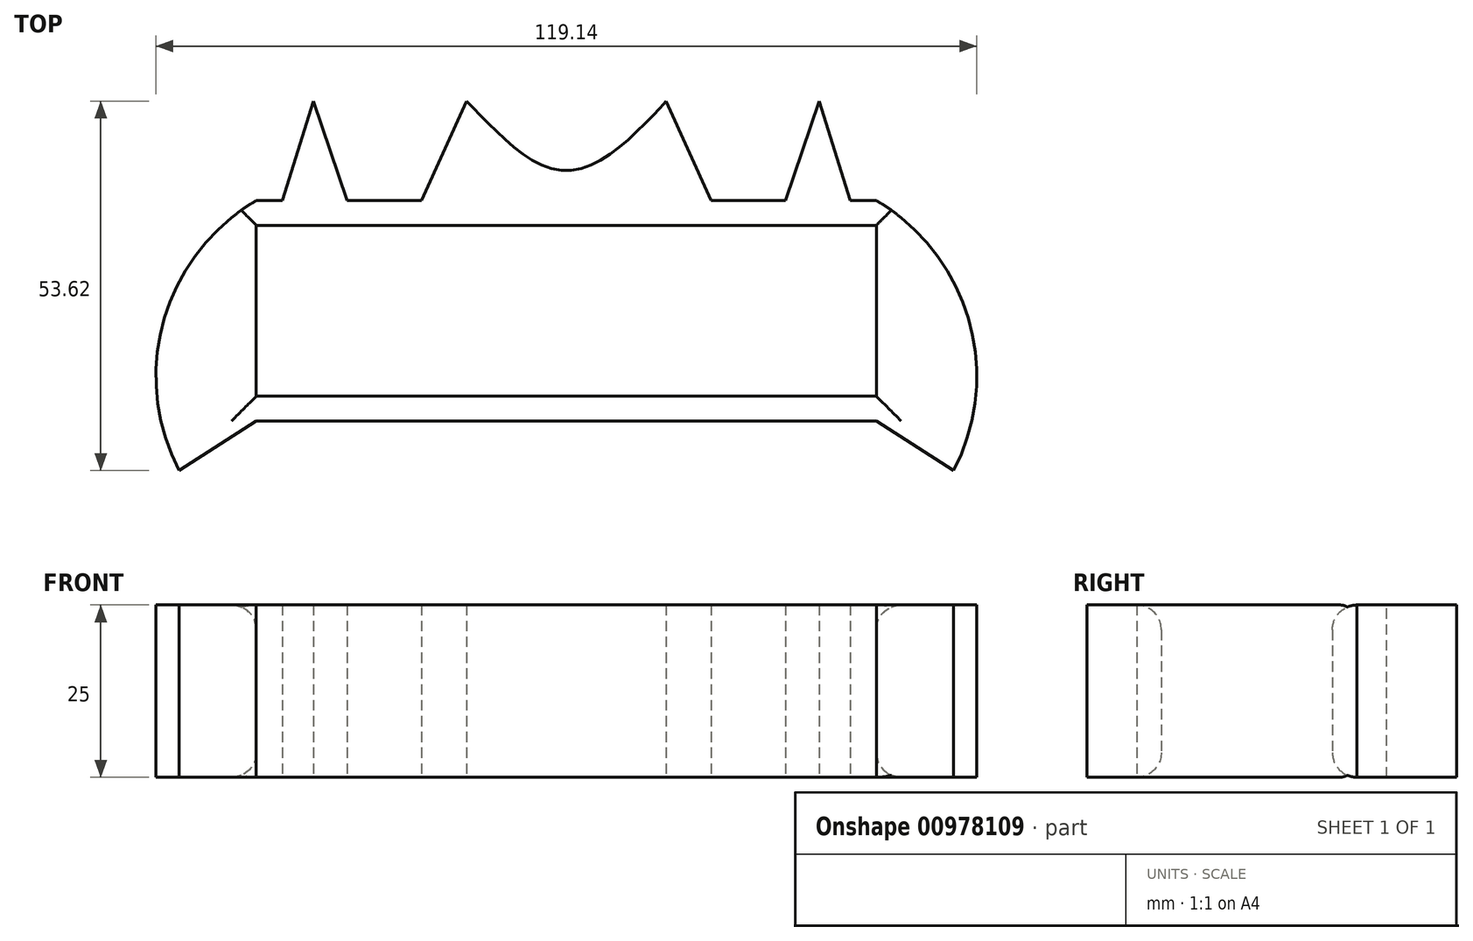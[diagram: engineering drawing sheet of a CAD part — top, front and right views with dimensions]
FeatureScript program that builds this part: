
annotation { "Feature Type Name" : "Feature", "Feature Type Description" : "" }
export const myFeature = defineFeature(function(context is Context, id is Id, definition is map)
    precondition{}
    {
        {
            var Q0;
            Q0=qCreatedBy(makeId("Top.planeOp"),FACE);
            var sketch = newSketch(context, id + "F0", { "sketchPlane" : qUnion([Q0])});
            skLineSegment(sketch, "E0.bottom", {"start": v(45, -16) * mm, "end": v(-45, -16) * mm});
            skLineSegment(sketch, "E0.top", {"start": v(45, 16) * mm, "end": v(-45, 16) * mm});
            skLineSegment(sketch, "E0.left", {"start": v(45, -16) * mm, "end": v(45, 16) * mm});
            skLineSegment(sketch, "E0.right", {"start": v(-45, -16) * mm, "end": v(-45, 16) * mm});
            skPoint(sketch, "E0.middle", {"position": v(0, 0) * mm});
            skPoint(sketch, "E1.centerSnap0", {"position": v(-45, 0) * mm});
            skFitSpline(sketch, "E2", {"points": [v(-14.5, 30.42) * mm, v(0, 20.32) * mm, v(14.5, 30.42) * mm], "startDerivative": vector(21.98, -21.4) * mm, "endDerivative": vector(20.35, 21.58) * mm});
            skLineSegment(sketch, "E3", {"start": v(14.5, 30.42) * mm, "end": v(21, 16) * mm});
            skLineSegment(sketch, "E4.MirrorCS", {"start": v(-14.5, 30.42) * mm, "end": v(-21, 16) * mm});
            skArc(sketch, "E5", {"start": v(56.2, -23.2) * mm, "mid": v(58.43, -1.36) * mm, "end": v(45, 16) * mm});
            skLineSegment(sketch, "E6", {"start": v(45, -16) * mm, "end": v(56.2, -23.2) * mm});
            skArc(sketch, "E7.MirrorCS", {"start": v(-56.2, -23.2) * mm, "mid": v(-58.43, -1.36) * mm, "end": v(-45, 16) * mm});
            skLineSegment(sketch, "E8.MirrorCS", {"start": v(-45, -16) * mm, "end": v(-56.2, -23.2) * mm});
            skLineSegment(sketch, "E9", {"start": v(-45, 12.4) * mm, "end": v(45, 12.4) * mm});
            skLineSegment(sketch, "E10", {"start": v(45, -12.4) * mm, "end": v(-45, -12.4) * mm});
            skPoint(sketch, "E11.end.orphan", {"position": v(-37, 16) * mm});
            skPoint(sketch, "E12.end.orphan", {"position": v(-43.48, 30.42) * mm});
            skPoint(sketch, "E12.start.orphan", {"position": v(-50, 16) * mm});
            skPoint(sketch, "E13.MirrorCS.end.orphan", {"position": v(43.48, 30.42) * mm});
            skPoint(sketch, "E13.MirrorCS.start.orphan", {"position": v(50, 16) * mm});
            skPoint(sketch, "E14.MirrorCS.end.orphan", {"position": v(37, 16) * mm});
            skLineSegment(sketch, "E15", {"start": v(-41.22, 16) * mm, "end": v(-36.7, 30.42) * mm});
            skLineSegment(sketch, "E16", {"start": v(-36.7, 30.42) * mm, "end": v(-31.81, 16) * mm});
            skLineSegment(sketch, "E17.MirrorCS", {"start": v(36.7, 30.42) * mm, "end": v(31.81, 16) * mm});
            skLineSegment(sketch, "E18.MirrorCS", {"start": v(41.22, 16) * mm, "end": v(36.7, 30.42) * mm});
            skPoint(sketch, "E19.MirrorC.center.orphan", {"position": v(14.5, 0) * mm});
            skPoint(sketch, "E1.center.orphan", {"position": v(-43.5, 0) * mm});
            skPoint(sketch, "E20.center.orphan", {"position": v(-14.5, 0) * mm});
            skSolve(sketch);
        }
        {
            var Q0;
            Q0=makeQuery(id+"F0.imprint","IMPRINT",FACE,{"disambiguationData":[TD([[makeQuery(id+"F0.imprint","IMPRINT",EDGE,{"derivedFrom":sQuery(id+"F0.wireOp",EDGE,"E0.right")}),1.0]])]});
            var Q1;
            Q1=makeQuery(id+"F0.imprint","IMPRINT",FACE,{"disambiguationData":[TD([[makeQuery(id+"F0.imprint","IMPRINT",EDGE,{"derivedFrom":sQuery(id+"F0.wireOp",EDGE,"E0.bottom")}),-1.0]])]});
            var Q2;
            {var subQ0=sQuery(id+"F0.wireOp",EDGE,"E12");Q2=makeQuery(id+"F0.imprint","IMPRINT",FACE,{"disambiguationData":[TD([[makeQuery(id+"F0.imprint","IMPRINT",EDGE,{"derivedFrom":subQ0}),-1.0]])]});}
            var Q3;
            Q3=makeQuery(id+"F0.imprint","IMPRINT",FACE,{"disambiguationData":[TD([[makeQuery(id+"F0.imprint","IMPRINT",EDGE,{"derivedFrom":sQuery(id+"F0.wireOp",EDGE,"E2")}),-1.0]])]});
            var Q4;
            {var subQ0=sQuery(id+"F0.wireOp",EDGE,"E14.MirrorCS");Q4=makeQuery(id+"F0.imprint","IMPRINT",FACE,{"disambiguationData":[TD([[makeQuery(id+"F0.imprint","IMPRINT",EDGE,{"derivedFrom":subQ0}),1.0]])]});}
            var Q5;
            Q5=makeQuery(id+"F0.imprint","IMPRINT",FACE,{"disambiguationData":[TD([[makeQuery(id+"F0.imprint","IMPRINT",EDGE,{"derivedFrom":sQuery(id+"F0.wireOp",EDGE,"E0.left")}),-1.0]])]});
            var Q6;
            {var subQ8=sQuery(id+"F0.wireOp",EDGE,"E19.MirrorC");Q6=makeQuery(id+"F0.imprint","IMPRINT",FACE,{"disambiguationData":[TD([[makeQuery(id+"F0.imprint","IMPRINT",EDGE,{"derivedFrom":subQ8}),1.0]])]});}
            var Q7;
            {var subQ0=sQuery(id+"F0.wireOp",EDGE,"E15");Q7=makeQuery(id+"F0.imprint","IMPRINT",FACE,{"disambiguationData":[TD([[makeQuery(id+"F0.imprint","IMPRINT",EDGE,{"derivedFrom":subQ0}),-1.0]])]});}
            var Q8;
            {var subQ0=sQuery(id+"F0.wireOp",EDGE,"E17.MirrorCS");Q8=makeQuery(id+"F0.imprint","IMPRINT",FACE,{"disambiguationData":[TD([[makeQuery(id+"F0.imprint","IMPRINT",EDGE,{"derivedFrom":subQ0}),1.0]])]});}
            var Q9;
            {var subQ7=sQuery(id+"F0.wireOp",EDGE,"E9");Q9=makeQuery(id+"F0.imprint","IMPRINT",FACE,{"disambiguationData":[TD([[makeQuery(id+"F0.imprint","IMPRINT",EDGE,{"derivedFrom":subQ7}),1.0]])]});}
            extrude(context, id + "F1", {"entities" : qUnion([Q0, Q1, Q2, Q3, Q4, Q5, Q6, Q7, Q8, Q9]), "depth" : 25 * mm, "offsetDistance" : 25 * mm});
        }
        {
            var Q0;
            Q0=makeQuery(id+"F1.opExtrude","CAP_EDGE",EDGE,{"disambiguationData":[OSD([sQuery(id+"F0.wireOp",EDGE,"E9")])],"isStart":false});
            var Q1;
            Q1=makeQuery(id+"F1.opExtrude","CAP_EDGE",EDGE,{"disambiguationData":[OSD([sQuery(id+"F0.wireOp",EDGE,"E9")])],"isStart":true});
            var Q2;
            Q2=makeQuery(id+"F1.opExtrude","CAP_EDGE",EDGE,{"disambiguationData":[OSD([sQuery(id+"F0.wireOp",EDGE,"E10")])],"isStart":true});
            var Q3;
            Q3=makeQuery(id+"F1.opExtrude","CAP_EDGE",EDGE,{"disambiguationData":[OSD([sQuery(id+"F0.wireOp",EDGE,"E10")])],"isStart":false});
            var Q4;
            Q4=makeQuery(id+"F1.opExtrude","CAP_EDGE",EDGE,{"disambiguationData":[OSD([sQuery(id+"F0.wireOp",EDGE,"E0.right")])],"isStart":false});
            var Q5;
            Q5=makeQuery(id+"F1.opExtrude","CAP_EDGE",EDGE,{"disambiguationData":[OSD([sQuery(id+"F0.wireOp",EDGE,"E0.right")])],"isStart":true});
            var Q6;
            Q6=makeQuery(id+"F1.opExtrude","CAP_EDGE",EDGE,{"disambiguationData":[OSD([sQuery(id+"F0.wireOp",EDGE,"E0.left")])],"isStart":false});
            var Q7;
            Q7=makeQuery(id+"F1.opExtrude","CAP_EDGE",EDGE,{"disambiguationData":[OSD([sQuery(id+"F0.wireOp",EDGE,"E0.left")])],"isStart":true});
            fillet(context, id + "F2", {"entities" : qUnion([Q0, Q1, Q2, Q3, Q4, Q5, Q6, Q7]), "radius" : 3.59 * mm, "tangentPropagation" : true, "allowEdgeOverflow" : false});
        }
    });
